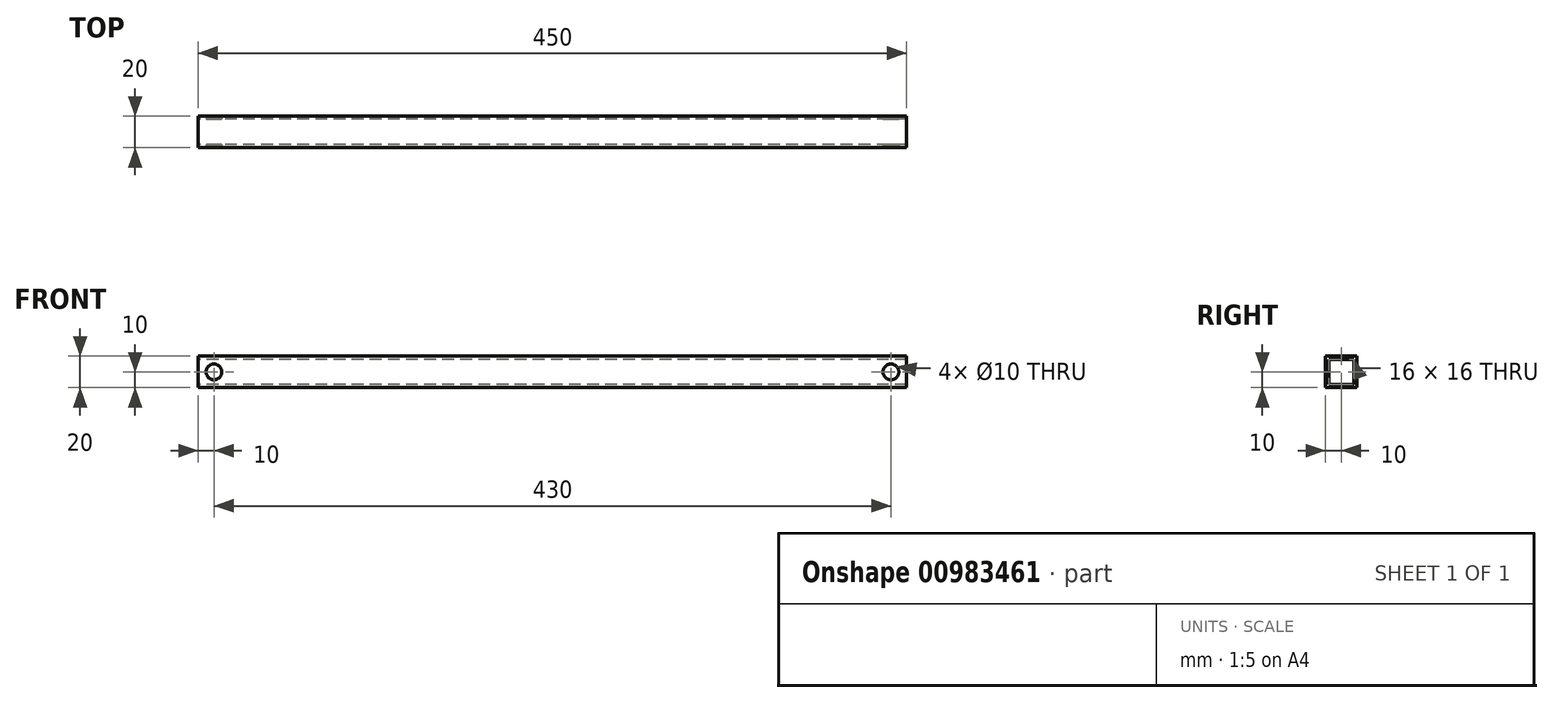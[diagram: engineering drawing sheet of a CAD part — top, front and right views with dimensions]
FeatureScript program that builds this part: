
annotation { "Feature Type Name" : "Feature", "Feature Type Description" : "" }
export const myFeature = defineFeature(function(context is Context, id is Id, definition is map)
    precondition{}
    {
        {
            var Q0;
            Q0=qCreatedBy(makeId("Right.planeOp"),FACE);
            var sketch = newSketch(context, id + "F0", { "sketchPlane" : qUnion([Q0])});
            skLineSegment(sketch, "E0.bottom", {"start": v(0, 0) * mm, "end": v(20, 0) * mm});
            skLineSegment(sketch, "E0.top", {"start": v(0, 20) * mm, "end": v(20, 20) * mm});
            skLineSegment(sketch, "E0.left", {"start": v(0, 0) * mm, "end": v(0, 20) * mm});
            skLineSegment(sketch, "E0.right", {"start": v(20, 0) * mm, "end": v(20, 20) * mm});
            skLineSegment(sketch, "E1.0", {"start": v(2, 18) * mm, "end": v(18, 18) * mm});
            skLineSegment(sketch, "E1.1", {"start": v(2, 2) * mm, "end": v(2, 18) * mm});
            skLineSegment(sketch, "E1.2", {"start": v(2, 2) * mm, "end": v(18, 2) * mm});
            skLineSegment(sketch, "E1.3", {"start": v(18, 2) * mm, "end": v(18, 18) * mm});
            skSolve(sketch);
        }
        {
            var Q0;
            Q0=qSketchRegion(id+"F0",true);
            extrude(context, id + "F1", {"entities" : qUnion([Q0]), "depth" : 450 * mm});
        }
        {
            var Q0;
            Q0=makeQuery(id+"F1.opExtrude","SWEPT_FACE",FACE,{"disambiguationData":[OSD([sQuery(id+"F0.wireOp",EDGE,"E0.left")])]});
            var sketch = newSketch(context, id + "F2", { "sketchPlane" : qUnion([Q0])});
            skCircle(sketch, "E2", {"center": v(440, 10) * mm, "radius": 5 * mm});
            skSolve(sketch);
        }
        {
            var Q0;
            Q0=qSketchRegion(id+"F2",true);
            extrude(context, id + "F3", {"entities" : qUnion([Q0]), "operationType" : NewBodyOperationType.REMOVE, "endBound" : BoundingType.THROUGH_ALL, "oppositeDirection" : true, "depth" : 25 * mm});
        }
        {
            var Q0;
            Q0=makeQuery(id+"F1.opExtrude","SWEPT_FACE",FACE,{"disambiguationData":[OSD([sQuery(id+"F0.wireOp",EDGE,"E0.left")])]});
            var sketch = newSketch(context, id + "F4", { "sketchPlane" : qUnion([Q0])});
            skCircle(sketch, "E3", {"center": v(10, 10) * mm, "radius": 5 * mm});
            skSolve(sketch);
        }
        {
            var Q0;
            Q0=qSketchRegion(id+"F4",true);
            extrude(context, id + "F5", {"entities" : qUnion([Q0]), "operationType" : NewBodyOperationType.REMOVE, "endBound" : BoundingType.THROUGH_ALL, "oppositeDirection" : true, "depth" : 25 * mm});
        }
    });
